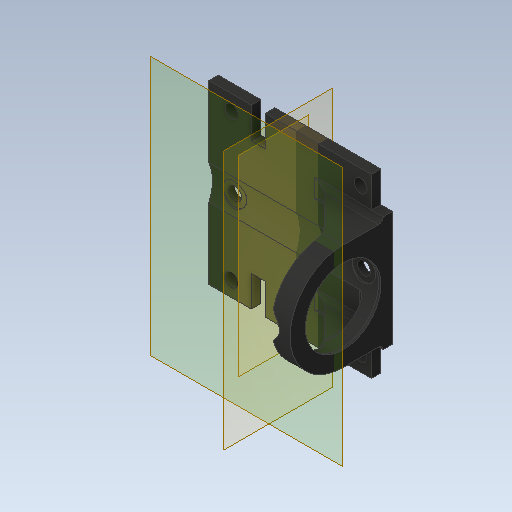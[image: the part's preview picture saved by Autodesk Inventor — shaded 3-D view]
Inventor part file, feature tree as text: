
AUTODESK INVENTOR PART (.ipt)
format: ipt  version: 2020 (Build 240168000, 168)  size: 736,256 bytes
history: native  units: mm
features: sketch x42, extrude x38, chamfer x6, pattern_linear x5, fillet x5, other x4, mirror x2
ambient origin geometry x8: Origin, YZ Plane, XZ Plane, XY Plane, X Axis, Y Axis, Z Axis, Center Point
bodies: Body1 (feature_tree)
feature tree (102):
  other  "Bryła1"
  extrude  "Wyciągnięcie proste1"  Depth=74.0mm
  extrude  "Wyciągnięcie proste2"  Depth=74.0mm
  extrude  "Wyciągnięcie proste3"  Depth=25.0mm TaperAngle=0.0deg
  extrude  "Wyciągnięcie proste4"  Depth=20.0mm
  other  "Płaszczyzna konstrukcyjna1"
  extrude  "Wyciągnięcie proste5"  Depth=20.0mm
  pattern_linear  "Szyk prostokątny1"  Spacing1=11.0mm  [1 undecoded]
  chamfer  "Faza1"  Distance=11.0mm
  chamfer  "Faza2"  Distance=19.8mm
  chamfer  "Faza3"  Distance=2.05mm
  extrude  "Wyciągnięcie proste6"  Depth=7.9mm
  extrude  "Wyciągnięcie proste7"  TaperAngle=0.0deg  [1 undecoded]
  extrude  "Wyciągnięcie proste8"  TaperAngle=0.0deg  [1 undecoded]
  extrude  "Wyciągnięcie proste9"  Depth=2.05mm
  extrude  "Wyciągnięcie proste10"  Depth=7.9mm
  extrude  "Wyciągnięcie proste11"  TaperAngle=0.0deg  [1 undecoded]
  pattern_linear  "Szyk prostokątny2"  Spacing1=0.0mm  [1 undecoded]
  extrude  "Wyciągnięcie proste12"  Depth=1.9mm TaperAngle=0.0deg
  other  "Płaszczyzna konstrukcyjna2"
  mirror  "Odbij1"
  chamfer  "Faza4"  Distance=4.0mm
  extrude  "Wyciągnięcie proste13"  Depth=5.5mm
  pattern_linear  "Szyk prostokątny3"  Spacing1=5.5mm  [1 undecoded]
  extrude  "Wyciągnięcie proste14"  Depth=6.0mm
  pattern_linear  "Szyk prostokątny4"  Spacing1=6.0mm  [1 undecoded]
  extrude  "Wyciągnięcie proste15"  Depth=54.78mm
  pattern_linear  "Szyk prostokątny5"  Spacing1=-37.0mm  [1 undecoded]
  extrude  "Wyciągnięcie proste16"  Depth=27.39mm
  other  "Płaszczyzna konstrukcyjna3"
  mirror  "Odbij2"
  extrude  "Wyciągnięcie proste17"  Depth=50.0mm TaperAngle=0.0deg
  extrude  "Wyciągnięcie proste18"  Depth=30.0mm
  extrude  "Wyciągnięcie proste19"  Depth=2.0mm TaperAngle=45.0deg
  extrude  "Wyciągnięcie proste20"  Depth=2.0mm TaperAngle=45.0deg
  extrude  "Wyciągnięcie proste21"  Depth=2.0mm TaperAngle=45.0deg
  chamfer  "Faza5"  Distance=22.9mm
  extrude  "Wyciągnięcie proste23"  Depth=12.0mm
  extrude  "Wyciągnięcie proste25"  Depth=12.0mm
  sketch  "Szkic28"
  extrude  "Wyciągnięcie proste26"  Depth=100.0mm
  extrude  "Wyciągnięcie proste24"  Depth=13.0mm
  extrude  "Wyciągnięcie proste27"  Depth=13.0mm
  chamfer  "Faza6"  Distance=25.0mm
  fillet  "Zaokrąglenie1"  Radius=25.0mm
  extrude  "Wyciągnięcie proste28"  Depth=25.0mm
  fillet  "Zaokrąglenie2"  Radius=55.0mm
  sketch  "Szkic32"
  extrude  "Wyciągnięcie proste29"  TaperAngle=0.0deg  [1 undecoded]
  extrude  "Wyciągnięcie proste30"  Depth=0.5mm
  extrude  "Wyciągnięcie proste32"  Depth=0.5mm
  extrude  "Wyciągnięcie proste33"  Depth=74.0mm TaperAngle=0.0deg
  extrude  "Wyciągnięcie proste34"  Depth=55.0mm TaperAngle=0.0deg
  sketch  "Szkic40"
  extrude  "Wyciągnięcie proste37"  Depth=55.0mm TaperAngle=0.0deg
  extrude  "Wyciągnięcie proste38"  Depth=3.5mm
  extrude  "Wyciągnięcie proste39"  Depth=13.1mm
  fillet  "Zaokrąglenie3"  Radius=13.0mm
  extrude  "Wyciągnięcie proste40"  Depth=5000.0mm TaperAngle=0.0deg
  sketch  "Szkic45"
  extrude  "Wyciągnięcie proste41"  Depth=30.0mm
  extrude  "Wyciągnięcie proste42"  Depth=11.0mm
  fillet  "Zaokrąglenie4"  Radius=11.0mm
  fillet  "Zaokrąglenie5"  Radius=5.0mm
  sketch  "Szkic1"
  sketch  "Szkic2"
  sketch  "Szkic3"
  sketch  "Szkic4"
  sketch  "Szkic5"
  sketch  "Szkic6"
  sketch  "Szkic7"
  sketch  "Szkic8"
  sketch  "Szkic9"
  sketch  "Szkic10"
  sketch  "Szkic12"
  sketch  "Szkic13"
  sketch  "Szkic15"
  sketch  "Szkic16"
  sketch  "Szkic17"
  sketch  "Szkic18"
  sketch  "Szkic19"
  sketch  "Szkic20"
  sketch  "Szkic21"
  sketch  "Szkic22"
  sketch  "Szkic23"
  sketch  "Szkic25"
  sketch  "Szkic26"
  sketch  "Szkic27"
  sketch  "Szkic29"
  sketch  "Szkic30"
  sketch  "Szkic31"
  sketch  "Szkic33"
  sketch  "Szkic34"
  sketch  "Szkic35"
  sketch  "Szkic36"
  sketch  "Szkic37"
  sketch  "Szkic41"
  sketch  "Szkic42"
  sketch  "Szkic43"
  sketch  "Szkic44"
  sketch  "Szkic46"
  sketch  "Szkic47"
note: 9 required parameter values undecoded (feature->parameter linkage not recoverable at this tier; creation-order binding heuristic only, values carry confidence <= 0.55)
